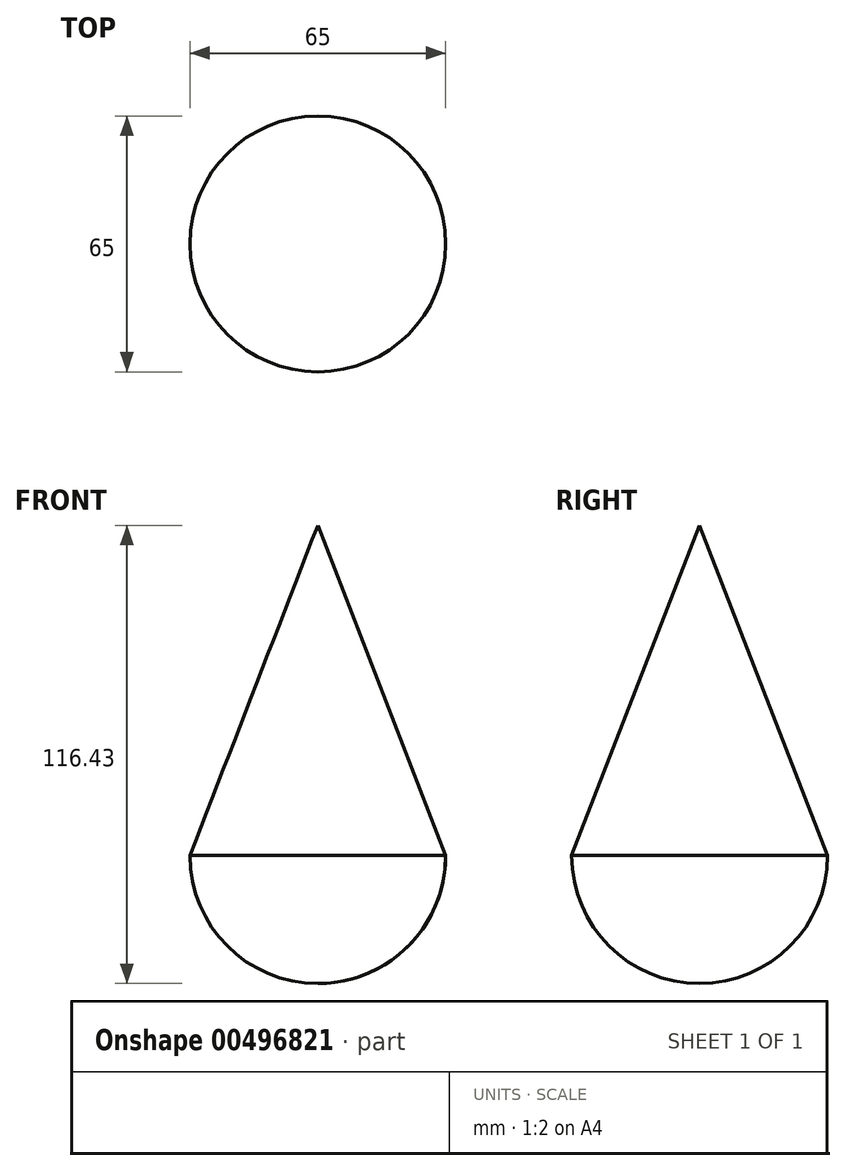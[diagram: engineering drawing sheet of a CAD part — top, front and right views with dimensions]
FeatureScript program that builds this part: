
annotation { "Feature Type Name" : "Feature", "Feature Type Description" : "" }
export const myFeature = defineFeature(function(context is Context, id is Id, definition is map)
    precondition{}
    {
        {
            var Q0;
            Q0=qCreatedBy(makeId("Front.planeOp"),FACE);
            var sketch = newSketch(context, id + "F0", { "sketchPlane" : qUnion([Q0])});
            skPoint(sketch, "E0.end.orphan", {"position": v(0, -32.55) * mm});
            skPoint(sketch, "E1.end.orphan", {"position": v(0, 99.3) * mm});
            skLineSegment(sketch, "E2", {"start": v(32.5, 0) * mm, "end": v(0, 83.93) * mm});
            skArc(sketch, "E3", {"start": v(0, -32.5) * mm, "mid": v(22.98, -22.98) * mm, "end": v(32.5, 0) * mm});
            skLineSegment(sketch, "E4", {"start": v(0, 0) * mm, "end": v(0, -32.55) * mm});
            skLineSegment(sketch, "E5", {"start": v(0, 83.93) * mm, "end": v(0, 23.93) * mm});
            skLineSegment(sketch, "E6", {"start": v(0, 23.93) * mm, "end": v(0, 0) * mm});
            skLineSegment(sketch, "E7", {"start": v(0, 23.93) * mm, "end": v(23.23, 23.93) * mm, "construction": true});
            skSolve(sketch);
        }
        {
            var Q0;
            Q0=makeQuery(id+"F0.imprint","IMPRINT",FACE,{"disambiguationData":[TD([[makeQuery(id+"F0.imprint","IMPRINT",EDGE,{"derivedFrom":sQuery(id+"F0.wireOp",EDGE,"E2")}),1.0]])]});
            var Q1;
            Q1=sQuery(id+"F0.wireOp",EDGE,"E6");
            revolve(context, id + "F1", {"surfaceOperationType" : NewSurfaceOperationType.NEW, "entities" : qUnion([Q0]), "axis" : qUnion([Q1]), "revolveType" : RevolveType.FULL});
        }
    });
